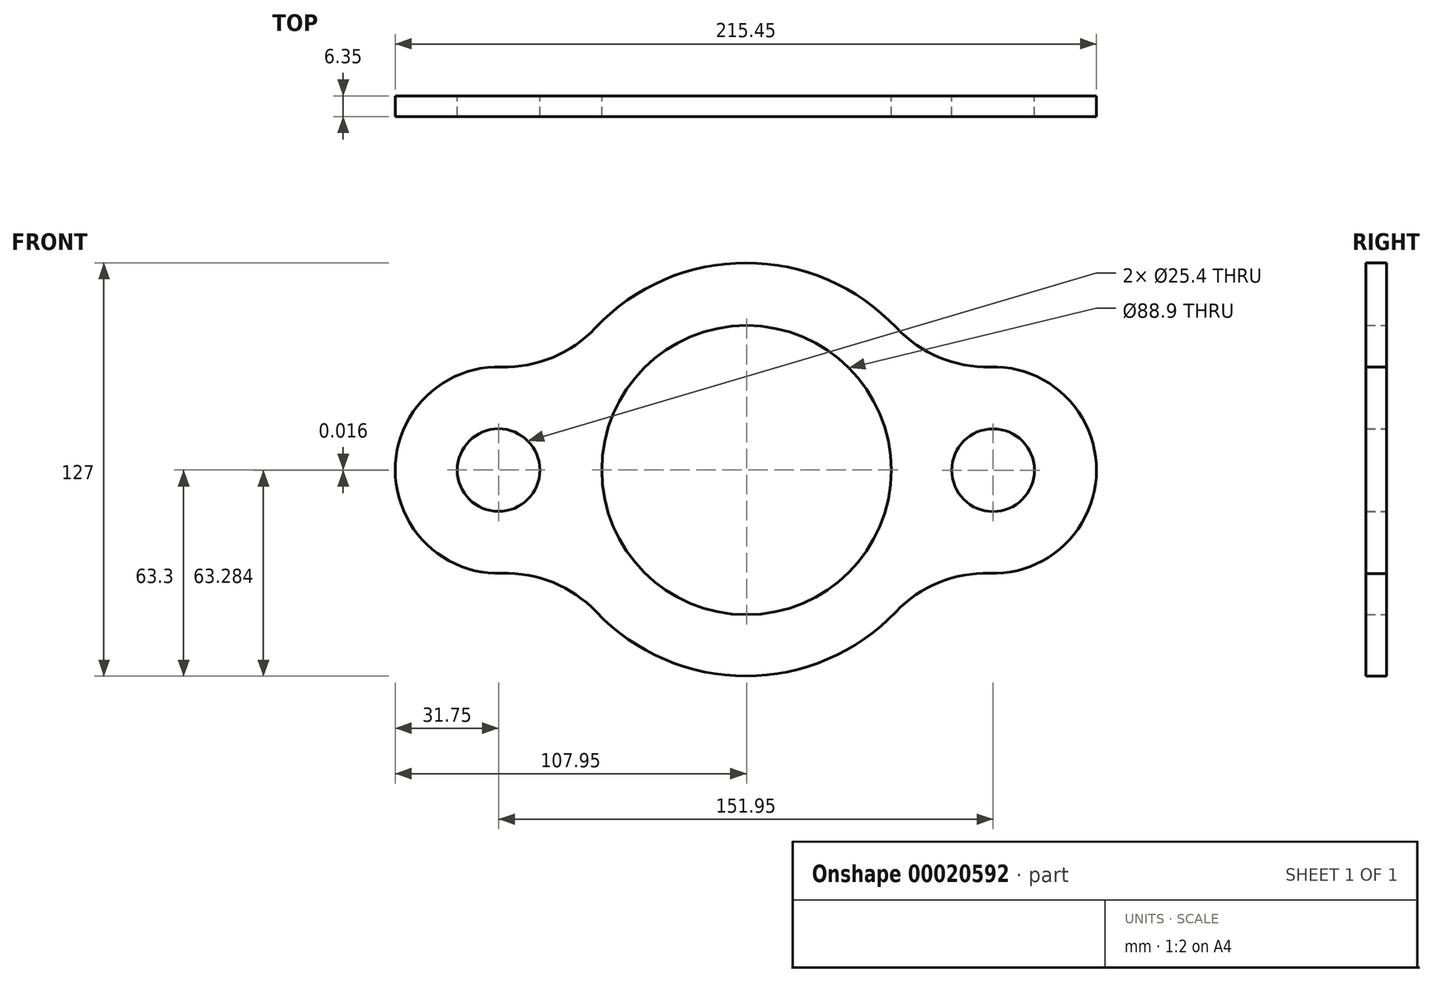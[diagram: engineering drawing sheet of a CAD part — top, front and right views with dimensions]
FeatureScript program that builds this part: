
annotation { "Feature Type Name" : "Feature", "Feature Type Description" : "" }
export const myFeature = defineFeature(function(context is Context, id is Id, definition is map)
    precondition{}
    {
        {
            var Q0;
            Q0=qCreatedBy(makeId("Front.planeOp"),FACE);
            var sketch = newSketch(context, id + "F0", { "sketchPlane" : qUnion([Q0])});
            skCircle(sketch, "E0", {"center": v(75.75, -0.02) * mm, "radius": 12.7 * mm});
            skArc(sketch, "E1", {"start": v(-75.28, 31.74) * mm, "mid": v(-107.95, -0.08) * mm, "end": v(-75.11, -31.73) * mm});
            skArc(sketch, "E2", {"start": v(74.7, -31.75) * mm, "mid": v(107.5, -0.1) * mm, "end": v(74.88, 31.72) * mm});
            skArc(sketch, "E3.trimOffspring", {"start": v(-46.2, -43.56) * mm, "mid": v(-0.19, -63.3) * mm, "end": v(45.83, -43.57) * mm});
            skArc(sketch, "E4.trimOffspring", {"start": v(46.08, 43.7) * mm, "mid": v(-0.17, 63.7) * mm, "end": v(-46.43, 43.71) * mm});
            skArc(sketch, "E5.filletArc", {"start": v(-75.28, 31.74) * mm, "mid": v(-59.57, 34.63) * mm, "end": v(-46.43, 43.71) * mm});
            skArc(sketch, "E6.filletArc", {"start": v(46.08, 43.7) * mm, "mid": v(59.2, 34.63) * mm, "end": v(74.88, 31.72) * mm});
            skArc(sketch, "E7.filletArc", {"start": v(-46.2, -43.56) * mm, "mid": v(-59.39, -34.54) * mm, "end": v(-75.11, -31.73) * mm});
            skArc(sketch, "E8.filletArc", {"start": v(74.7, -31.75) * mm, "mid": v(59, -34.57) * mm, "end": v(45.83, -43.57) * mm});
            skCircle(sketch, "E9", {"center": v(0, 0) * mm, "radius": 44.45 * mm});
            skCircle(sketch, "E10", {"center": v(-76.2, 0) * mm, "radius": 12.7 * mm});
            skSolve(sketch);
        }
        {
            var Q0;
            Q0 = qSketchRegion(id + "F0", true);
            extrude(context, id + "F1", {"entities" : qUnion([Q0]), "depth" : 6.35 * mm});
        }
    });
